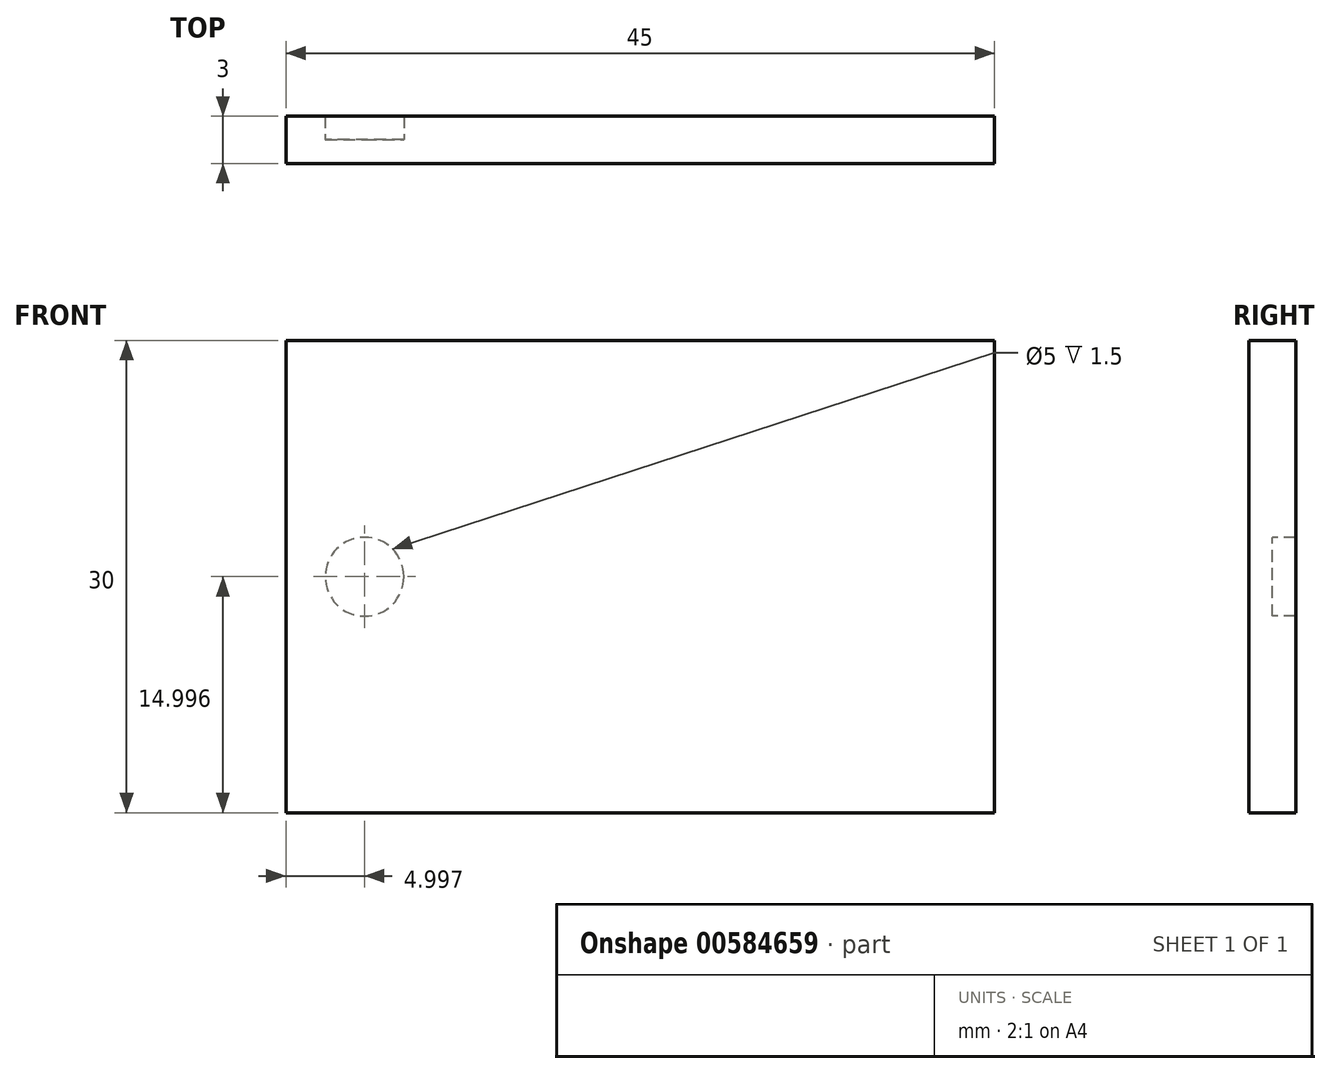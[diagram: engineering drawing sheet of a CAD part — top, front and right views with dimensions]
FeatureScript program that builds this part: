
annotation { "Feature Type Name" : "Feature", "Feature Type Description" : "" }
export const myFeature = defineFeature(function(context is Context, id is Id, definition is map)
    precondition{}
    {
        {
            var Q0;
            Q0=qCreatedBy(makeId("Front.planeOp"),FACE);
            var sketch = newSketch(context, id + "F0", { "sketchPlane" : qUnion([Q0])});
            skLineSegment(sketch, "E0.bottom", {"start": v(12.72, -4.84) * mm, "end": v(-32.28, -4.84) * mm});
            skLineSegment(sketch, "E0.top", {"start": v(12.72, 25.16) * mm, "end": v(-32.28, 25.16) * mm});
            skLineSegment(sketch, "E0.left", {"start": v(12.72, -4.84) * mm, "end": v(12.72, 25.16) * mm});
            skLineSegment(sketch, "E0.right", {"start": v(-32.28, -4.84) * mm, "end": v(-32.28, 25.16) * mm});
            skPoint(sketch, "E0.middle", {"position": v(-9.78, 10.16) * mm});
            skPoint(sketch, "E1", {"position": v(-27.28, 10.16) * mm});
            skPoint(sketch, "E2", {"position": v(7.72, 10.16) * mm});
            skSolve(sketch);
        }
        {
            var Q0;
            Q0=makeQuery(id+"F0.imprint","IMPRINT",FACE,{"disambiguationData":[TD([[makeQuery(id+"F0.imprint","IMPRINT",EDGE,{"derivedFrom":sQuery(id+"F0.wireOp",EDGE,"E0.bottom")}),-1.0]])]});
            extrude(context, id + "F1", {"entities" : qUnion([Q0]), "endBound" : BoundingType.SYMMETRIC, "depth" : 3 * mm, "offsetDistance" : 25 * mm});
        }
        {
            var Q0;
            Q0=sQuery(id+"F0.wireOp",VERTEX,"E1");
            var Q1;
            Q1=makeQuery(id+"F1.opExtrude","SWEPT_BODY",BODY,{"disambiguationData":[OSD([sQuery(id+"F0.wireOp",EDGE,"E0.bottom"),sQuery(id+"F0.wireOp",EDGE,"E0.top"),sQuery(id+"F0.wireOp",EDGE,"E0.left"),sQuery(id+"F0.wireOp",EDGE,"E0.right")])]});
            hole(context, id + "F2", {"style" : HoleStyle.SIMPLE, "endStyle" : HoleEndStyle.THROUGH, "holeDiameter" : 5 * mm, "majorDiameter" : 5 * mm, "isTappedThrough" : true, "tappedDepth" : 12 * mm, "tapClearance" : 3, "locations" : qUnion([Q0]), "scope" : qUnion([Q1])});
        }
    });
